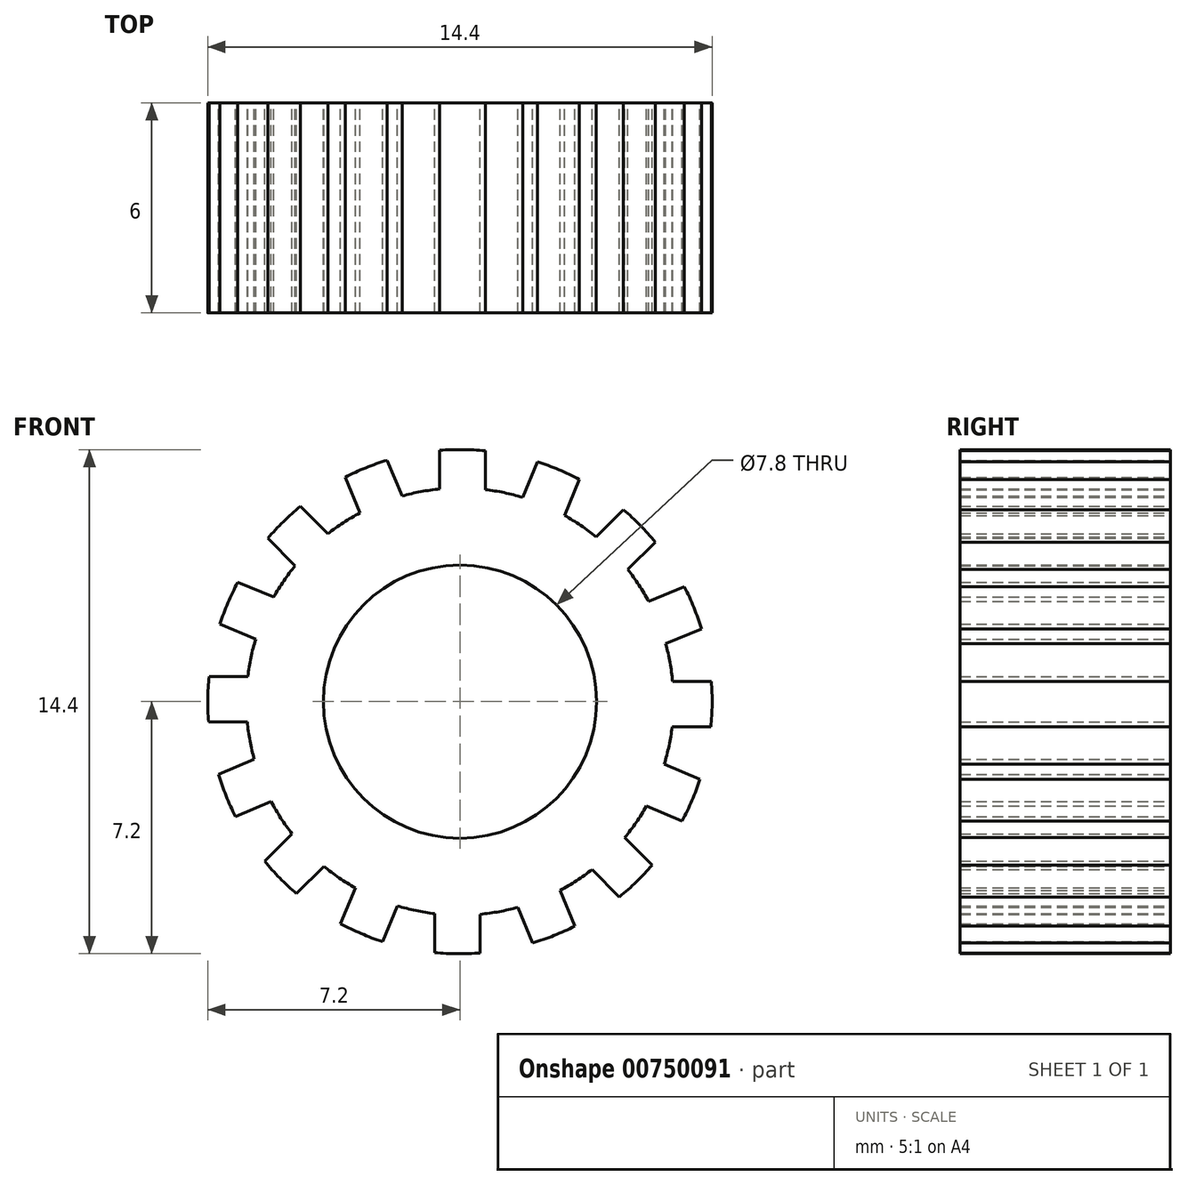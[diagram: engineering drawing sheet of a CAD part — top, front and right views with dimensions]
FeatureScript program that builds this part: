
annotation { "Feature Type Name" : "Feature", "Feature Type Description" : "" }
export const myFeature = defineFeature(function(context is Context, id is Id, definition is map)
    precondition{}
    {
        {
            var Q0;
            Q0=qCreatedBy(makeId("Front.planeOp"),FACE);
            var sketch = newSketch(context, id + "F0", { "sketchPlane" : qUnion([Q0])});
            skCircle(sketch, "E0", {"center": v(0, 0) * mm, "radius": 3.9 * mm});
            skArc(sketch, "E1", {"start": v(-2.07, 6.9) * mm, "mid": v(-2.69, 6.68) * mm, "end": v(-3.28, 6.4) * mm});
            skCircle(sketch, "E2", {"center": v(0, 0) * mm, "radius": 6.1 * mm});
            skLineSegment(sketch, "E3", {"start": v(-0.58, 6.07) * mm, "end": v(-0.58, 7.18) * mm});
            skLineSegment(sketch, "E4", {"start": v(0.72, 6.06) * mm, "end": v(0.72, 7.16) * mm});
            skArc(sketch, "E5", {"start": v(0.72, 7.16) * mm, "mid": v(0.07, 7.2) * mm, "end": v(-0.58, 7.18) * mm});
            skArc(sketch, "E6", {"start": v(0.72, 6.06) * mm, "mid": v(0.07, 6.1) * mm, "end": v(-0.58, 6.07) * mm});
            skLineSegment(sketch, "E7.1.0", {"start": v(-1.65, 5.87) * mm, "end": v(-2.07, 6.9) * mm});
            skLineSegment(sketch, "E7.1.1", {"start": v(-2.86, 5.39) * mm, "end": v(-3.28, 6.4) * mm});
            skArc(sketch, "E7.1.3", {"start": v(-1.65, 5.87) * mm, "mid": v(-2.27, 5.67) * mm, "end": v(-2.86, 5.39) * mm});
            skLineSegment(sketch, "E7.2.0", {"start": v(-3.77, 4.8) * mm, "end": v(-4.56, 5.58) * mm});
            skLineSegment(sketch, "E7.2.1", {"start": v(-4.7, 3.89) * mm, "end": v(-5.48, 4.67) * mm});
            skArc(sketch, "E7.2.2", {"start": v(-4.56, 5.58) * mm, "mid": v(-5.04, 5.14) * mm, "end": v(-5.48, 4.67) * mm});
            skArc(sketch, "E7.2.3", {"start": v(-3.77, 4.8) * mm, "mid": v(-4.26, 4.37) * mm, "end": v(-4.7, 3.89) * mm});
            skLineSegment(sketch, "E7.3.0", {"start": v(-5.32, 2.98) * mm, "end": v(-6.34, 3.4) * mm});
            skLineSegment(sketch, "E7.3.1", {"start": v(-5.83, 1.79) * mm, "end": v(-6.85, 2.21) * mm});
            skArc(sketch, "E7.3.2", {"start": v(-6.34, 3.4) * mm, "mid": v(-6.62, 2.82) * mm, "end": v(-6.85, 2.21) * mm});
            skArc(sketch, "E7.3.3", {"start": v(-5.32, 2.98) * mm, "mid": v(-5.61, 2.4) * mm, "end": v(-5.83, 1.79) * mm});
            skLineSegment(sketch, "E7.4.0", {"start": v(-6.06, 0.72) * mm, "end": v(-7.16, 0.72) * mm});
            skLineSegment(sketch, "E7.4.1", {"start": v(-6.07, -0.58) * mm, "end": v(-7.18, -0.58) * mm});
            skArc(sketch, "E7.4.2", {"start": v(-7.16, 0.72) * mm, "mid": v(-7.2, 0.07) * mm, "end": v(-7.18, -0.58) * mm});
            skArc(sketch, "E7.4.3", {"start": v(-6.06, 0.72) * mm, "mid": v(-6.1, 0.07) * mm, "end": v(-6.07, -0.58) * mm});
            skLineSegment(sketch, "E7.5.0", {"start": v(-5.87, -1.65) * mm, "end": v(-6.9, -2.07) * mm});
            skLineSegment(sketch, "E7.5.1", {"start": v(-5.39, -2.86) * mm, "end": v(-6.4, -3.28) * mm});
            skArc(sketch, "E7.5.2", {"start": v(-6.9, -2.07) * mm, "mid": v(-6.68, -2.69) * mm, "end": v(-6.4, -3.28) * mm});
            skArc(sketch, "E7.5.3", {"start": v(-5.87, -1.65) * mm, "mid": v(-5.67, -2.27) * mm, "end": v(-5.39, -2.86) * mm});
            skLineSegment(sketch, "E7.6.0", {"start": v(-4.8, -3.77) * mm, "end": v(-5.58, -4.56) * mm});
            skLineSegment(sketch, "E7.6.1", {"start": v(-3.89, -4.7) * mm, "end": v(-4.67, -5.48) * mm});
            skArc(sketch, "E7.6.2", {"start": v(-5.58, -4.56) * mm, "mid": v(-5.14, -5.04) * mm, "end": v(-4.67, -5.48) * mm});
            skArc(sketch, "E7.6.3", {"start": v(-4.8, -3.77) * mm, "mid": v(-4.37, -4.26) * mm, "end": v(-3.89, -4.7) * mm});
            skLineSegment(sketch, "E7.7.0", {"start": v(-2.98, -5.32) * mm, "end": v(-3.4, -6.34) * mm});
            skLineSegment(sketch, "E7.7.1", {"start": v(-1.79, -5.83) * mm, "end": v(-2.21, -6.85) * mm});
            skArc(sketch, "E7.7.2", {"start": v(-3.4, -6.34) * mm, "mid": v(-2.82, -6.62) * mm, "end": v(-2.21, -6.85) * mm});
            skArc(sketch, "E7.7.3", {"start": v(-2.98, -5.32) * mm, "mid": v(-2.4, -5.61) * mm, "end": v(-1.79, -5.83) * mm});
            skLineSegment(sketch, "E7.8.0", {"start": v(-0.72, -6.06) * mm, "end": v(-0.72, -7.16) * mm});
            skLineSegment(sketch, "E7.8.1", {"start": v(0.58, -6.07) * mm, "end": v(0.58, -7.18) * mm});
            skArc(sketch, "E7.8.2", {"start": v(-0.72, -7.16) * mm, "mid": v(-0.07, -7.2) * mm, "end": v(0.58, -7.18) * mm});
            skArc(sketch, "E7.8.3", {"start": v(-0.72, -6.06) * mm, "mid": v(-0.07, -6.1) * mm, "end": v(0.58, -6.07) * mm});
            skLineSegment(sketch, "E7.9.0", {"start": v(1.65, -5.87) * mm, "end": v(2.07, -6.9) * mm});
            skLineSegment(sketch, "E7.9.1", {"start": v(2.86, -5.39) * mm, "end": v(3.28, -6.4) * mm});
            skArc(sketch, "E7.9.2", {"start": v(2.07, -6.9) * mm, "mid": v(2.69, -6.68) * mm, "end": v(3.28, -6.4) * mm});
            skArc(sketch, "E7.9.3", {"start": v(1.65, -5.87) * mm, "mid": v(2.27, -5.67) * mm, "end": v(2.86, -5.39) * mm});
            skLineSegment(sketch, "E7.10.0", {"start": v(3.77, -4.8) * mm, "end": v(4.56, -5.58) * mm});
            skLineSegment(sketch, "E7.10.1", {"start": v(4.7, -3.89) * mm, "end": v(5.48, -4.67) * mm});
            skArc(sketch, "E7.10.2", {"start": v(4.56, -5.58) * mm, "mid": v(5.04, -5.14) * mm, "end": v(5.48, -4.67) * mm});
            skArc(sketch, "E7.10.3", {"start": v(3.77, -4.8) * mm, "mid": v(4.26, -4.37) * mm, "end": v(4.7, -3.89) * mm});
            skLineSegment(sketch, "E7.11.0", {"start": v(5.32, -2.98) * mm, "end": v(6.34, -3.4) * mm});
            skLineSegment(sketch, "E7.11.1", {"start": v(5.83, -1.79) * mm, "end": v(6.85, -2.21) * mm});
            skArc(sketch, "E7.11.2", {"start": v(6.34, -3.4) * mm, "mid": v(6.62, -2.82) * mm, "end": v(6.85, -2.21) * mm});
            skArc(sketch, "E7.11.3", {"start": v(5.32, -2.98) * mm, "mid": v(5.61, -2.4) * mm, "end": v(5.83, -1.79) * mm});
            skLineSegment(sketch, "E7.12.0", {"start": v(6.06, -0.72) * mm, "end": v(7.16, -0.72) * mm});
            skLineSegment(sketch, "E7.12.1", {"start": v(6.07, 0.58) * mm, "end": v(7.18, 0.58) * mm});
            skArc(sketch, "E7.12.2", {"start": v(7.16, -0.72) * mm, "mid": v(7.2, -0.07) * mm, "end": v(7.18, 0.58) * mm});
            skArc(sketch, "E7.12.3", {"start": v(6.06, -0.72) * mm, "mid": v(6.1, -0.07) * mm, "end": v(6.07, 0.58) * mm});
            skLineSegment(sketch, "E7.13.0", {"start": v(5.87, 1.65) * mm, "end": v(6.9, 2.07) * mm});
            skLineSegment(sketch, "E7.13.1", {"start": v(5.39, 2.86) * mm, "end": v(6.4, 3.28) * mm});
            skArc(sketch, "E7.13.2", {"start": v(6.9, 2.07) * mm, "mid": v(6.68, 2.69) * mm, "end": v(6.4, 3.28) * mm});
            skArc(sketch, "E7.13.3", {"start": v(5.87, 1.65) * mm, "mid": v(5.67, 2.27) * mm, "end": v(5.39, 2.86) * mm});
            skLineSegment(sketch, "E7.14.0", {"start": v(4.8, 3.77) * mm, "end": v(5.58, 4.56) * mm});
            skLineSegment(sketch, "E7.14.1", {"start": v(3.89, 4.7) * mm, "end": v(4.67, 5.48) * mm});
            skArc(sketch, "E7.14.2", {"start": v(5.58, 4.56) * mm, "mid": v(5.14, 5.04) * mm, "end": v(4.67, 5.48) * mm});
            skArc(sketch, "E7.14.3", {"start": v(4.8, 3.77) * mm, "mid": v(4.37, 4.26) * mm, "end": v(3.89, 4.7) * mm});
            skLineSegment(sketch, "E7.15.0", {"start": v(2.98, 5.32) * mm, "end": v(3.4, 6.34) * mm});
            skLineSegment(sketch, "E7.15.1", {"start": v(1.79, 5.83) * mm, "end": v(2.21, 6.85) * mm});
            skArc(sketch, "E7.15.2", {"start": v(3.4, 6.34) * mm, "mid": v(2.82, 6.62) * mm, "end": v(2.21, 6.85) * mm});
            skArc(sketch, "E7.15.3", {"start": v(2.98, 5.32) * mm, "mid": v(2.4, 5.61) * mm, "end": v(1.79, 5.83) * mm});
            skSolve(sketch);
        }
        {
            var Q0;
            Q0 = qSketchRegion(id + "F0", true);
            extrude(context, id + "F1", {"entities" : qUnion([Q0]), "depth" : 6 * mm, "offsetDistance" : 25 * mm});
        }
    });
